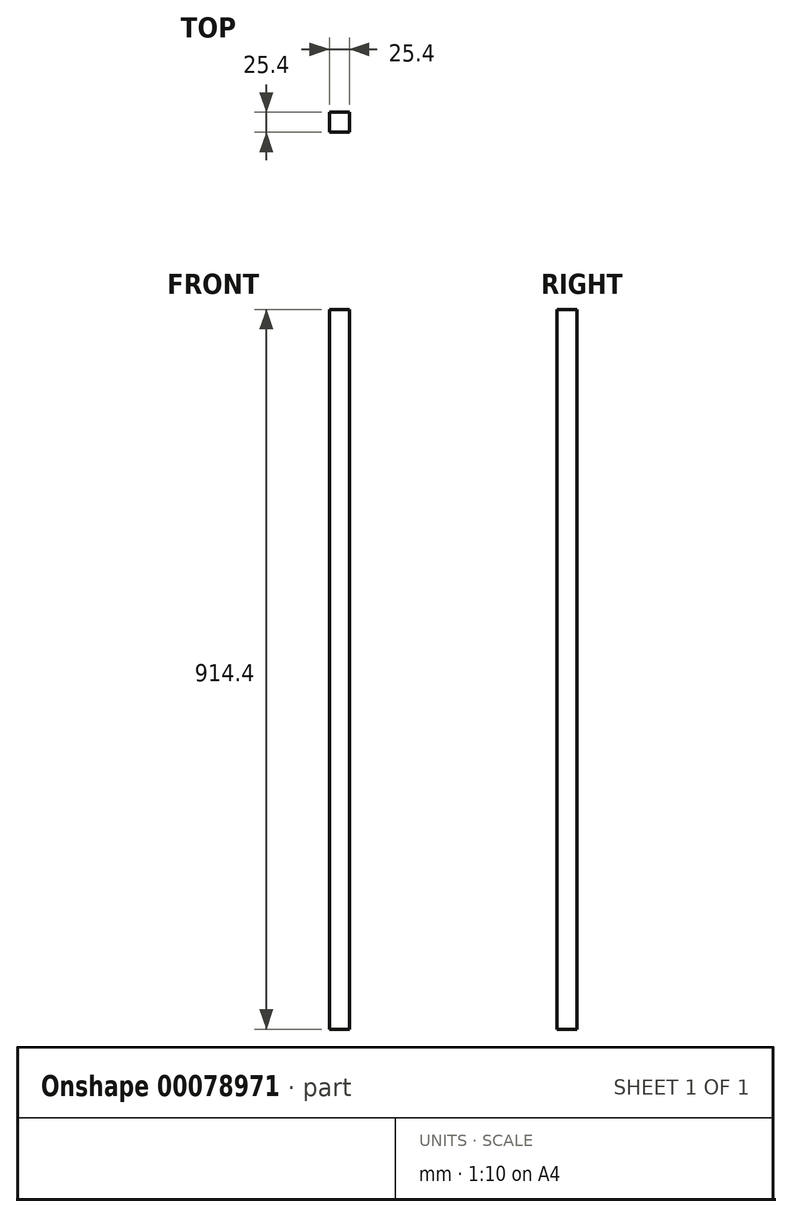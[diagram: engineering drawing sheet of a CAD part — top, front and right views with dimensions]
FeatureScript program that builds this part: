
annotation { "Feature Type Name" : "Feature", "Feature Type Description" : "" }
export const myFeature = defineFeature(function(context is Context, id is Id, definition is map)
    precondition{}
    {
        {
            var Q0;
            Q0=qCreatedBy(makeId("Top.planeOp"),FACE);
            var sketch = newSketch(context, id + "F0", { "sketchPlane" : qUnion([Q0])});
            skLineSegment(sketch, "E0.bottom", {"start": v(-12.7, 12.7) * mm, "end": v(12.7, 12.7) * mm});
            skLineSegment(sketch, "E0.top", {"start": v(-12.7, -12.7) * mm, "end": v(12.7, -12.7) * mm});
            skLineSegment(sketch, "E0.left", {"start": v(-12.7, 12.7) * mm, "end": v(-12.7, -12.7) * mm});
            skLineSegment(sketch, "E0.right", {"start": v(12.7, 12.7) * mm, "end": v(12.7, -12.7) * mm});
            skPoint(sketch, "E0.middle", {"position": v(0, 0) * mm});
            skSolve(sketch);
        }
        {
            var Q0;
            Q0=makeQuery(id+"F0.imprint","IMPRINT",FACE,{"disambiguationData":[TD([[makeQuery(id+"F0.imprint","IMPRINT",EDGE,{"derivedFrom":sQuery(id+"F0.wireOp",EDGE,"E0.bottom")}),-1.0]])]});
            extrude(context, id + "F1", {"entities" : qUnion([Q0]), "depth" : 914.4 * mm});
        }
    });
